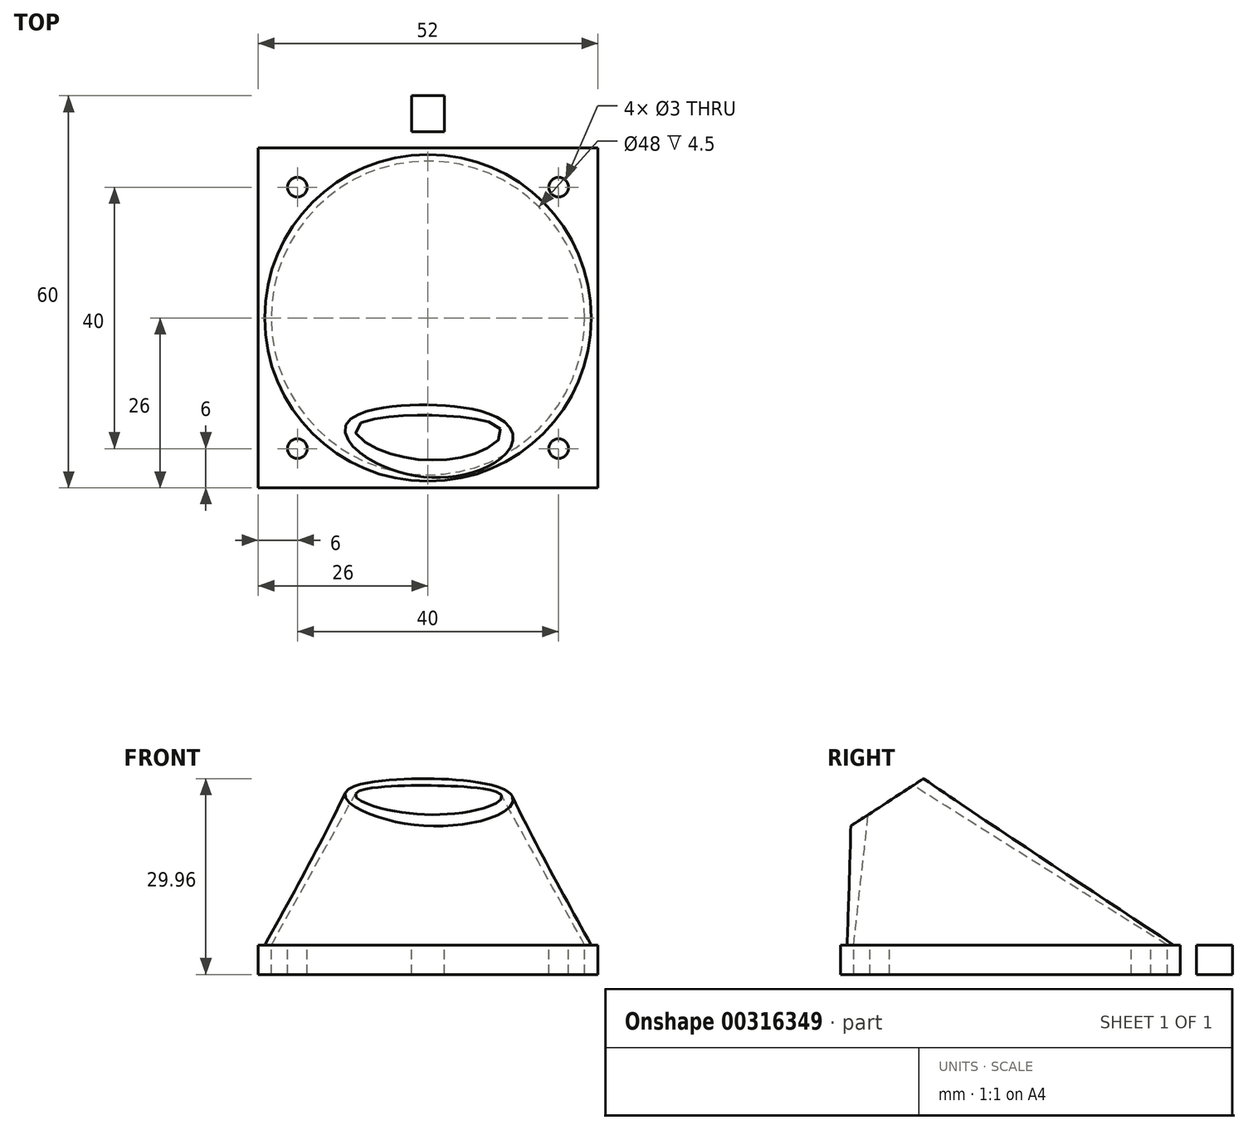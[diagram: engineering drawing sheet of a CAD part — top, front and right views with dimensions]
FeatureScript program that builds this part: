
annotation { "Feature Type Name" : "Feature", "Feature Type Description" : "" }
export const myFeature = defineFeature(function(context is Context, id is Id, definition is map)
    precondition{}
    {
        {
            var Q0;
            Q0=qCreatedBy(makeId("Top.planeOp"),FACE);
            var sketch = newSketch(context, id + "F0", { "sketchPlane" : qUnion([Q0])});
            skPoint(sketch, "E0.middle", {"position": v(0, 0) * mm});
            skCircle(sketch, "E1", {"center": v(0, 0) * mm, "radius": 24 * mm});
            skLineSegment(sketch, "E2.bottom", {"start": v(26, -26) * mm, "end": v(-26, -26) * mm});
            skLineSegment(sketch, "E2.top", {"start": v(26, 26) * mm, "end": v(-26, 26) * mm});
            skLineSegment(sketch, "E2.left", {"start": v(26, -26) * mm, "end": v(26, 26) * mm});
            skLineSegment(sketch, "E2.right", {"start": v(-26, -26) * mm, "end": v(-26, 26) * mm});
            skCircle(sketch, "E3", {"center": v(20, -20) * mm, "radius": 1.5 * mm});
            skCircle(sketch, "E4.MirrorC", {"center": v(-20, -20) * mm, "radius": 1.5 * mm});
            skCircle(sketch, "E5.MirrorC", {"center": v(20, 20) * mm, "radius": 1.5 * mm});
            skCircle(sketch, "E6.MirrorC", {"center": v(-20, 20) * mm, "radius": 1.5 * mm});
            skLineSegment(sketch, "E7.bottom", {"start": v(2.5, 26) * mm, "end": v(-2.5, 26) * mm});
            skLineSegment(sketch, "E7.top", {"start": v(2.5, 34) * mm, "end": v(-2.5, 34) * mm});
            skLineSegment(sketch, "E7.left", {"start": v(2.5, 26) * mm, "end": v(2.5, 34) * mm});
            skLineSegment(sketch, "E7.right", {"start": v(-2.5, 26) * mm, "end": v(-2.5, 34) * mm});
            skPoint(sketch, "E7.middle", {"position": v(0, 30) * mm});
            skLineSegment(sketch, "E8.0", {"start": v(2.5, 30) * mm, "end": v(-2.5, 30) * mm});
            skLineSegment(sketch, "E9.0", {"start": v(2.5, 31.5) * mm, "end": v(-2.5, 31.5) * mm});
            skLineSegment(sketch, "E10.0", {"start": v(2.5, 28.5) * mm, "end": v(-2.5, 28.5) * mm});
            skSolve(sketch);
        }
        {
            var Q0;
            Q0=qCreatedBy(makeId("Top.planeOp"),FACE);
            cPlane(context, id + "F1", {"entities" : qUnion([Q0]), "cplaneType" : CPlaneType.OFFSET, "offset" : 27 * mm, "width" : 150 * mm, "height" : 150 * mm});
        }
        {
            var Q0;
            Q0=qCreatedBy(id+"F1.planeOp",FACE);
            var sketch = newSketch(context, id + "F2", { "sketchPlane" : qUnion([Q0])});
            skEllipse(sketch, "E11", {"center": v(0, -20) * mm, "majorRadius": 9 * mm, "minorRadius": 1 * mm, "majorAxis": v(1, 0)});
            skSolve(sketch);
        }
        {
            var Q0;
            Q0=makeQuery(id+"F0.imprint","IMPRINT",FACE,{"disambiguationData":[TD([[makeQuery(id+"F0.imprint","IMPRINT",EDGE,{"derivedFrom":sQuery(id+"F0.wireOp",EDGE,"E1")}),1.0]])]});
            var Q1;
            Q1=makeQuery(id+"F2.imprint","IMPRINT",FACE,{"disambiguationData":[TD([[makeQuery(id+"F2.imprint","IMPRINT",EDGE,{"derivedFrom":sQuery(id+"F2.wireOp",EDGE,"E11")}),1.0]])]});
            loft(context, id + "F3", {"sheetProfilesArray" : [{ "sheetProfileEntities" : qUnion([Q0]) }, { "sheetProfileEntities" : qUnion([Q1]) }]});
        }
        {
            var Q0;
            Q0=qCreatedBy(makeId("Top.planeOp"),FACE);
            var sketch = newSketch(context, id + "F4", { "sketchPlane" : qUnion([Q0])});
            skCircle(sketch, "E12", {"center": v(0, 0) * mm, "radius": 25 * mm});
            skSolve(sketch);
        }
        {
            var Q0;
            Q0=qCreatedBy(id+"F1.planeOp",FACE);
            var sketch = newSketch(context, id + "F5", { "sketchPlane" : qUnion([Q0])});
            skEllipse(sketch, "E13", {"center": v(0, -20) * mm, "majorRadius": 11 * mm, "minorRadius": 4.5 * mm, "majorAxis": v(1, 0)});
            skSolve(sketch);
        }
        {
            var Q1;
            Q1=makeQuery(id+"F4.imprint","IMPRINT",FACE,{"disambiguationData":[TD([[makeQuery(id+"F4.imprint","IMPRINT",EDGE,{"derivedFrom":sQuery(id+"F4.wireOp",EDGE,"E12")}),1.0]])]});
            var Q2;
            Q2=makeQuery(id+"F5.imprint","IMPRINT",FACE,{"disambiguationData":[TD([[makeQuery(id+"F5.imprint","IMPRINT",EDGE,{"derivedFrom":sQuery(id+"F5.wireOp",EDGE,"E13")}),1.0]])]});
            loft(context, id + "F6", {"sheetProfilesArray" : [{ "sheetProfileEntities" : qUnion([Q1]) }, { "sheetProfileEntities" : qUnion([Q2]) }]});
        }
        {
            var Q0;
            Q0=makeQuery(id+"F3.opLoft","SWEPT_BODY",BODY,{"disambiguationData":[OSD([makeQuery(id+"F0.imprint","IMPRINT",FACE,{"disambiguationData":[TD([[makeQuery(id+"F0.imprint","IMPRINT",EDGE,{"derivedFrom":sQuery(id+"F0.wireOp",EDGE,"E1")}),1.0]])]}),makeQuery(id+"F2.imprint","IMPRINT",FACE,{"disambiguationData":[TD([[makeQuery(id+"F2.imprint","IMPRINT",EDGE,{"derivedFrom":sQuery(id+"F2.wireOp",EDGE,"E11")}),1.0]])]})])]});
            var Q1;
            Q1=makeQuery(id+"F6.opLoft","SWEPT_BODY",BODY,{"disambiguationData":[OSD([makeQuery(id+"F4.imprint","IMPRINT",FACE,{"disambiguationData":[TD([[makeQuery(id+"F4.imprint","IMPRINT",EDGE,{"derivedFrom":sQuery(id+"F4.wireOp",EDGE,"E12")}),1.0]])]}),makeQuery(id+"F5.imprint","IMPRINT",FACE,{"disambiguationData":[TD([[makeQuery(id+"F5.imprint","IMPRINT",EDGE,{"derivedFrom":sQuery(id+"F5.wireOp",EDGE,"E13")}),1.0]])]})])]});
            booleanBodies(context, id + "F7", {"operationType" : BooleanOperationType.SUBTRACTION, "tools" : qUnion([Q0]), "targets" : qUnion([Q1])});
        }
        {
            var Q0;
            Q0=makeQuery(id+"F0.imprint","IMPRINT",FACE,{"disambiguationData":[TD([[makeQuery(id+"F0.imprint","IMPRINT",EDGE,{"derivedFrom":sQuery(id+"F0.wireOp",EDGE,"E1")}),-1.0]])]});
            var Q1;
            {var subQ0=sQuery(id+"F0.wireOp",EDGE,"E7.bottom");Q1=makeQuery(id+"F0.imprint","IMPRINT",FACE,{"disambiguationData":[TD([[makeQuery(id+"F0.imprint","IMPRINT",EDGE,{"derivedFrom":subQ0}),-1.0]])]});}
            var Q2;
            {var subQ0=sQuery(id+"F0.wireOp",EDGE,"E8.0");Q2=makeQuery(id+"F0.imprint","IMPRINT",FACE,{"disambiguationData":[TD([[makeQuery(id+"F0.imprint","IMPRINT",EDGE,{"derivedFrom":subQ0}),1.0]])]});}
            var Q3;
            {var subQ0=sQuery(id+"F0.wireOp",EDGE,"E8.0");Q3=makeQuery(id+"F0.imprint","IMPRINT",FACE,{"disambiguationData":[TD([[makeQuery(id+"F0.imprint","IMPRINT",EDGE,{"derivedFrom":subQ0}),-1.0]])]});}
            var Q4;
            {var subQ0=sQuery(id+"F0.wireOp",EDGE,"E7.top");Q4=makeQuery(id+"F0.imprint","IMPRINT",FACE,{"disambiguationData":[TD([[makeQuery(id+"F0.imprint","IMPRINT",EDGE,{"derivedFrom":subQ0}),1.0]])]});}
            extrude(context, id + "F8", {"entities" : qUnion([Q0, Q1, Q2, Q3, Q4]), "operationType" : NewBodyOperationType.ADD, "oppositeDirection" : true, "depth" : 4.5 * mm});
        }
        {
            var Q0;
            {var subQ0=sQuery(id+"F0.wireOp",EDGE,"E8.0");Q0=makeQuery(id+"F0.imprint","IMPRINT",FACE,{"disambiguationData":[TD([[makeQuery(id+"F0.imprint","IMPRINT",EDGE,{"derivedFrom":subQ0}),1.0]])]});}
            var Q1;
            Q1=sQuery(id+"F0.wireOp",EDGE,"E8.0");
            revolve(context, id + "F9", {"entities" : qUnion([Q0]), "axis" : qUnion([Q1]), "revolveType" : RevolveType.FULL});
        }
        {
            var Q0;
            Q0=makeQuery(id+"F9.opRevolve","SWEPT_BODY",BODY,{"disambiguationData":[OSD([sQuery(id+"F0.wireOp",EDGE,"E7.left"),sQuery(id+"F0.wireOp",EDGE,"E7.right"),sQuery(id+"F0.wireOp",EDGE,"E8.0"),sQuery(id+"F0.wireOp",EDGE,"E10.0")])]});
            transform(context, id + "F10", {"entities" : qUnion([Q0]), "transformType" : TransformType.TRANSLATION_3D, "dx" : 0 * mm, "dy" : 0 * mm, "dz" : -2 * mm, "makeCopy" : false});
        }
        {
            var Q0;
            Q0=makeQuery(id+"F9.opRevolve","SWEPT_BODY",BODY,{"disambiguationData":[OSD([sQuery(id+"F0.wireOp",EDGE,"E7.left"),sQuery(id+"F0.wireOp",EDGE,"E7.right"),sQuery(id+"F0.wireOp",EDGE,"E8.0"),sQuery(id+"F0.wireOp",EDGE,"E10.0")])]});
            var Q1;
            Q1=makeQuery(id+"F6.opLoft","SWEPT_BODY",BODY,{"disambiguationData":[OSD([makeQuery(id+"F4.imprint","IMPRINT",FACE,{"disambiguationData":[TD([[makeQuery(id+"F4.imprint","IMPRINT",EDGE,{"derivedFrom":sQuery(id+"F4.wireOp",EDGE,"E12")}),1.0]])]}),makeQuery(id+"F5.imprint","IMPRINT",FACE,{"disambiguationData":[TD([[makeQuery(id+"F5.imprint","IMPRINT",EDGE,{"derivedFrom":sQuery(id+"F5.wireOp",EDGE,"E13")}),1.0]])]})])]});
            booleanBodies(context, id + "F11", {"operationType" : BooleanOperationType.SUBTRACTION, "tools" : qUnion([Q0]), "targets" : qUnion([Q1])});
        }
        {
            var Q0;
            Q0=qCreatedBy(makeId("Right.planeOp"),FACE);
            var sketch = newSketch(context, id + "F12", { "sketchPlane" : qUnion([Q0])});
            skLineSegment(sketch, "E14", {"start": v(-34, 12) * mm, "end": v(-9.4, 28) * mm});
            skLineSegment(sketch, "E15", {"start": v(-9.4, 28) * mm, "end": v(-9.4, 38) * mm});
            skLineSegment(sketch, "E16", {"start": v(-9.4, 38) * mm, "end": v(-34, 38) * mm});
            skLineSegment(sketch, "E17", {"start": v(-34, 38) * mm, "end": v(-34, 12) * mm});
            skSolve(sketch);
        }
        {
            var Q0;
            Q0=makeQuery(id+"F12.imprint","IMPRINT",FACE,{"disambiguationData":[TD([[makeQuery(id+"F12.imprint","IMPRINT",EDGE,{"derivedFrom":sQuery(id+"F12.wireOp",EDGE,"E14")}),1.0]])]});
            extrude(context, id + "F13", {"entities" : qUnion([Q0]), "operationType" : NewBodyOperationType.REMOVE, "depth" : 25 * mm, "hasSecondDirection" : true, "secondDirectionOppositeDirection" : true, "secondDirectionDepth" : 25 * mm});
        }
    });
